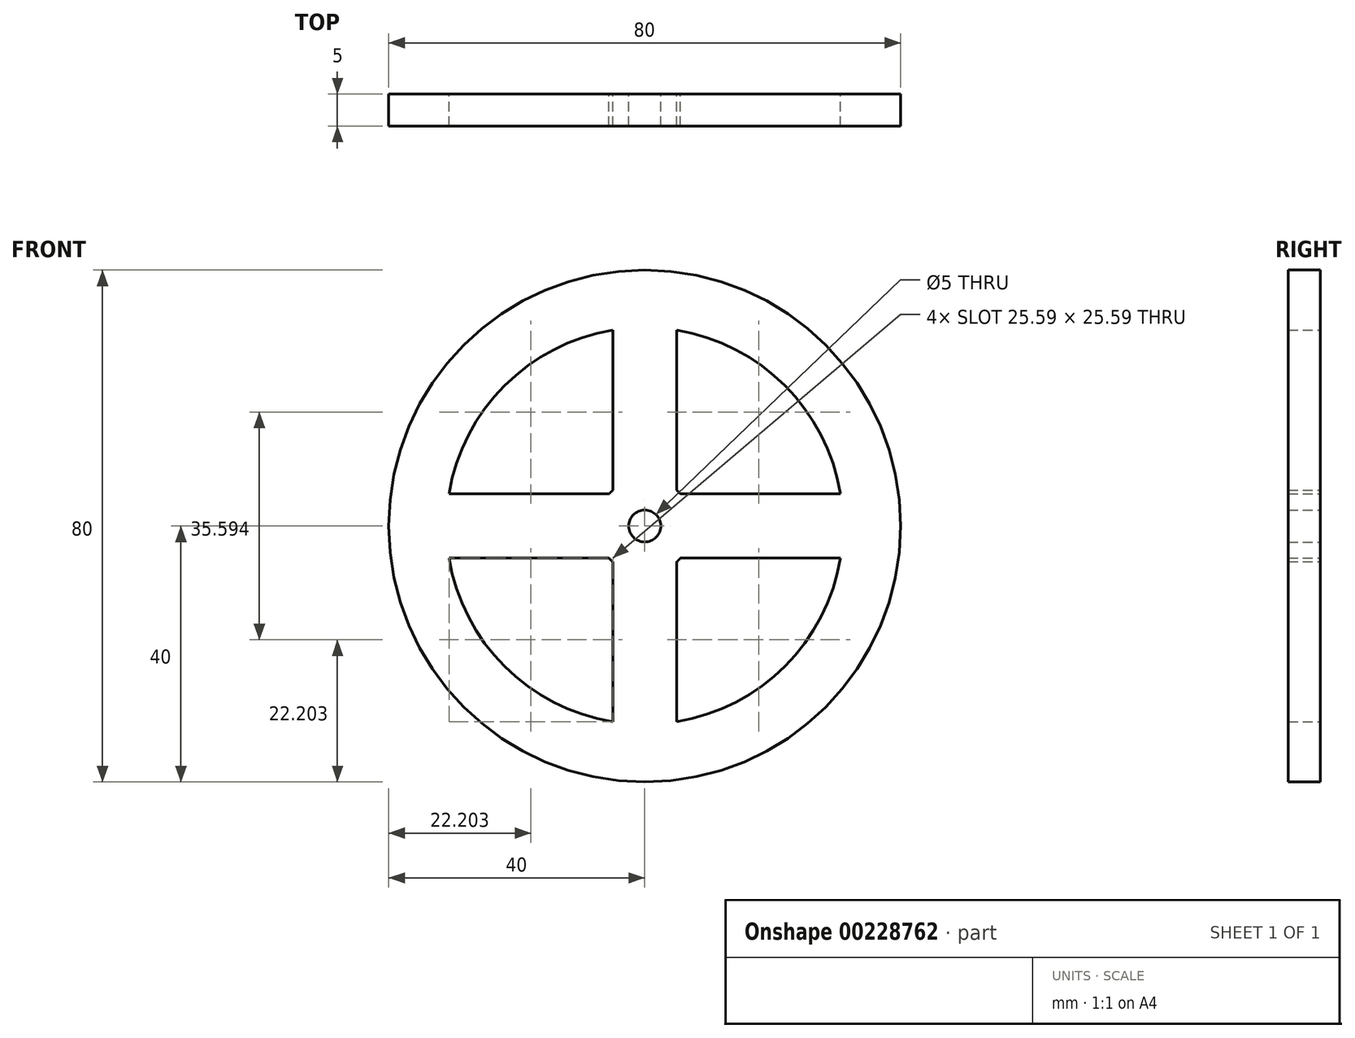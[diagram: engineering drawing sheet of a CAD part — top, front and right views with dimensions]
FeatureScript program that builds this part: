
annotation { "Feature Type Name" : "Feature", "Feature Type Description" : "" }
export const myFeature = defineFeature(function(context is Context, id is Id, definition is map)
    precondition{}
    {
        {
            var Q0;
            Q0=qCreatedBy(makeId("Front.planeOp"),FACE);
            var sketch = newSketch(context, id + "F0", { "sketchPlane" : qUnion([Q0])});
            skCircle(sketch, "E0", {"center": v(0, 0) * mm, "radius": 40 * mm});
            skArc(sketch, "E1", {"start": v(-30.6, -5) * mm, "mid": v(-21.92, -21.92) * mm, "end": v(-5, -30.6) * mm});
            skArc(sketch, "E2", {"start": v(5.6, 5) * mm, "mid": v(5.3, 5.3) * mm, "end": v(5, 5.6) * mm});
            skCircle(sketch, "E3", {"center": v(0, 0) * mm, "radius": 2.5 * mm});
            skLineSegment(sketch, "E4", {"start": v(0, 0) * mm, "end": v(0, 40) * mm, "construction": true});
            skLineSegment(sketch, "E5", {"start": v(0, 0) * mm, "end": v(40, 0) * mm, "construction": true});
            skLineSegment(sketch, "E6", {"start": v(0, 0) * mm, "end": v(0, -40) * mm, "construction": true});
            skLineSegment(sketch, "E7", {"start": v(0, 0) * mm, "end": v(-40, 0) * mm, "construction": true});
            skLineSegment(sketch, "E8.0", {"start": v(5, 5.6) * mm, "end": v(5, 30.6) * mm});
            skLineSegment(sketch, "E9.0", {"start": v(-5, 5.6) * mm, "end": v(-5, 30.6) * mm});
            skLineSegment(sketch, "E10.0", {"start": v(5.6, -5) * mm, "end": v(30.6, -5) * mm});
            skLineSegment(sketch, "E11.0", {"start": v(5.6, 5) * mm, "end": v(30.6, 5) * mm});
            skLineSegment(sketch, "E12.0", {"start": v(-5, -5.6) * mm, "end": v(-5, -30.6) * mm});
            skLineSegment(sketch, "E13.0", {"start": v(5, -5.6) * mm, "end": v(5, -30.6) * mm});
            skLineSegment(sketch, "E14.0", {"start": v(-5.6, -5) * mm, "end": v(-30.6, -5) * mm});
            skLineSegment(sketch, "E15.0", {"start": v(-5.6, 5) * mm, "end": v(-30.6, 5) * mm});
            skArc(sketch, "E16.trimOffspring", {"start": v(5, -30.6) * mm, "mid": v(21.92, -21.92) * mm, "end": v(30.6, -5) * mm});
            skArc(sketch, "E17.trimOffspring", {"start": v(30.6, 5) * mm, "mid": v(21.92, 21.92) * mm, "end": v(5, 30.6) * mm});
            skArc(sketch, "E18.trimOffspring", {"start": v(-5, 30.6) * mm, "mid": v(-21.92, 21.92) * mm, "end": v(-30.6, 5) * mm});
            skArc(sketch, "E19.trimOffspring", {"start": v(-5, 5.6) * mm, "mid": v(-5.3, 5.3) * mm, "end": v(-5.6, 5) * mm});
            skArc(sketch, "E20.trimOffspring", {"start": v(-5.6, -5) * mm, "mid": v(-5.3, -5.3) * mm, "end": v(-5, -5.6) * mm});
            skArc(sketch, "E21.trimOffspring", {"start": v(5, -5.6) * mm, "mid": v(5.3, -5.3) * mm, "end": v(5.6, -5) * mm});
            skSolve(sketch);
        }
        {
            var Q0;
            Q0=makeQuery(id+"F0.imprint","IMPRINT",FACE,{"disambiguationData":[TD([[makeQuery(id+"F0.imprint","IMPRINT",EDGE,{"derivedFrom":sQuery(id+"F0.wireOp",EDGE,"E0")}),1.0]])]});
            extrude(context, id + "F1", {"entities" : qUnion([Q0]), "endBound" : BoundingType.SYMMETRIC, "depth" : 5 * mm});
        }
    });
